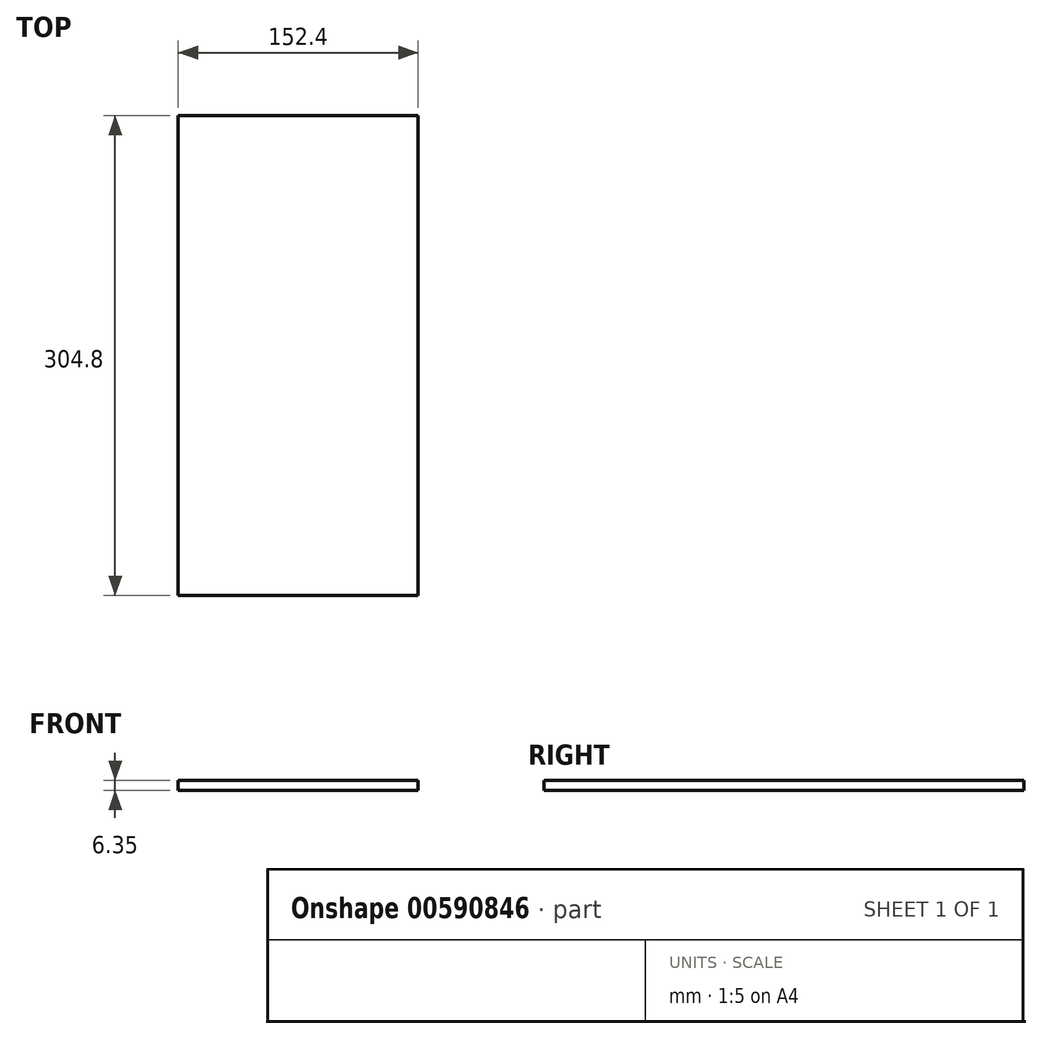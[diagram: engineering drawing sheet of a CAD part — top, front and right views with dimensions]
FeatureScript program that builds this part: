
annotation { "Feature Type Name" : "Feature", "Feature Type Description" : "" }
export const myFeature = defineFeature(function(context is Context, id is Id, definition is map)
    precondition{}
    {
        {
            var Q0;
            Q0=qCreatedBy(makeId("Top.planeOp"),FACE);
            var sketch = newSketch(context, id + "F0", { "sketchPlane" : qUnion([Q0])});
            skLineSegment(sketch, "E0", {"start": v(87.76, 207.9) * mm, "end": v(87.76, -96.9) * mm});
            skLineSegment(sketch, "E1", {"start": v(87.76, -96.9) * mm, "end": v(-64.64, -96.9) * mm});
            skLineSegment(sketch, "E2", {"start": v(-64.64, -96.9) * mm, "end": v(-64.64, 207.9) * mm});
            skLineSegment(sketch, "E3", {"start": v(-64.64, 207.9) * mm, "end": v(87.76, 207.9) * mm});
            skSolve(sketch);
        }
        {
            var Q0;
            Q0=makeQuery(id+"F0.imprint","IMPRINT",FACE,{"disambiguationData":[TD([[makeQuery(id+"F0.imprint","IMPRINT",EDGE,{"derivedFrom":sQuery(id+"F0.wireOp",EDGE,"E0")}),-1.0]])]});
            extrude(context, id + "F1", {"entities" : qUnion([Q0]), "depth" : 6.35 * mm, "offsetDistance" : 25.4 * mm});
        }
    });
